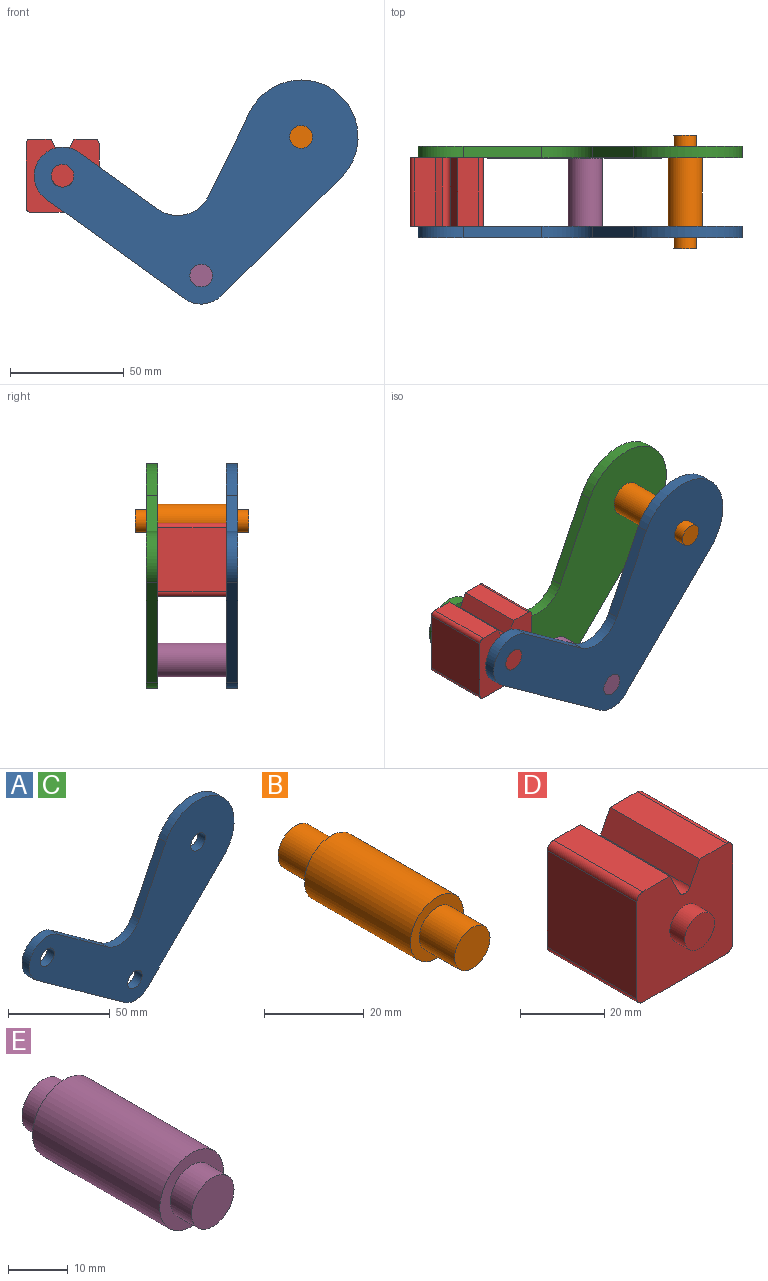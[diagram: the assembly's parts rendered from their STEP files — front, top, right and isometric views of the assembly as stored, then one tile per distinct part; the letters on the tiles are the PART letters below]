
ASSEMBLY  parts=5 mates=2
PART A: 13 faces, bbox 142.2x5x98.4 mm
  f0: plane 52.61x51.97mm, normal (0.7,0,-0.71), area 369.8mm2, adj f1,f9,f11,f12
  f1: cylinder r=25mm len=47.44mm, axis (0,-1,0), area 434.6mm2, adj f0,f2,f11,f12
  f2: plane 37.17x18.26mm, normal (-0.9,0,0.44), area 207.1mm2, adj f1,f3,f11,f12
  f3: cylinder r=15mm len=22.23mm, axis (0,-1,0), area 130.4mm2, adj f2,f4,f11,f12
  f4: plane 34.46x24.81mm, normal (0.58,0,0.81), area 212.3mm2, adj f3,f5,f11,f12
  f5: cylinder r=12.5mm len=22.64mm, axis (0,-1,0), area 196.3mm2, adj f4,f6,f11,f12
  f6: plane 60.86x43.82mm, normal (-0.58,0,-0.81), area 375mm2, adj f5,f9,f11,f12
  f7: cylinder r=5mm len=10mm, axis (0,-1,0), area 157.1mm2, adj f11,f12
  f8: cylinder r=5mm len=10mm, axis (0,-1,0), area 157.1mm2, adj f11,f12
  f9: cylinder r=12.5mm len=16.09mm, axis (0,-1,0), area 87.7mm2, adj f0,f6,f11,f12
  f10: cylinder r=5mm len=10mm, axis (0,-1,0), area 157.1mm2, adj f11,f12
  f11: plane 142.19x98.36mm, normal (0,1,0), area 5739.8mm2, adj f0,f1,f2,f3,f4,f5,f6,f7
  f12: plane 142.19x98.36mm, normal (0,-1,0), area 5739.8mm2, adj f0,f1,f2,f3,f4,f5,f6,f7
PART B: 7 faces, bbox 15x50x15 mm
  f0: cylinder r=7.5mm len=30mm, axis (0,-1,0), area 1413.7mm2, adj f2,f5
  f1: cylinder r=5mm len=10mm, axis (0,1,0), area 314.2mm2, adj f2,f3
  f2: plane 15x15mm, normal (0,-1,0), area 98.2mm2, adj f0,f1
  f3: plane 10x10mm, normal (0,-1,0), area 78.5mm2, adj f1
  f4: cylinder r=5mm len=10mm, axis (0,-1,0), area 314.2mm2, adj f5,f6
  f5: plane 15x15mm, normal (0,1,0), area 98.2mm2, adj f0,f4
  f6: plane 10x10mm, normal (0,1,0), area 78.5mm2, adj f4
PART C: same geometry as A
PART D: 18 faces, bbox 32.1x40x32.1 mm
  f0: plane 30x6.42mm, normal (0.89,0,0.45), area 215.4mm2, adj f4,f6,f10,f13
  f1: plane 30x6.42mm, normal (-0.89,0,0.45), area 215.4mm2, adj f2,f4,f10,f13
  f2: plane 30x9.04mm, normal (0,0,1), area 271.2mm2, adj f1,f4,f10,f14
  f3: plane 30x28.08mm, normal (1,0,0), area 842.3mm2, adj f4,f10,f14,f15
  f4: plane 32.08x32.08mm, normal (0,-1,0), area 900.6mm2, adj f0,f1,f2,f3,f5,f6,f7,f9
  f5: plane 30x28.08mm, normal (0,0,-1), area 842.3mm2, adj f4,f10,f15,f16
  f6: plane 30x9.04mm, normal (0,0,1), area 271.2mm2, adj f0,f4,f10,f17
  f7: plane 30x28.08mm, normal (-1,0,0), area 842.3mm2, adj f4,f10,f16,f17
  f8: plane 10x10mm, normal (0,-1,0), area 78.5mm2, adj f9
  f9: cylinder r=5mm len=10mm, axis (0,1,0), area 157.1mm2, adj f4,f8
  f10: plane 32.08x32.08mm, normal (0,1,0), area 900.6mm2, adj f0,f1,f2,f3,f5,f6,f7,f12
  f11: plane 10x10mm, normal (0,1,0), area 78.5mm2, adj f12
  f12: cylinder r=5mm len=10mm, axis (0,-1,0), area 157.1mm2, adj f10,f11
  f13: cylinder r=2mm len=30mm, axis (0,1,0), area 132.9mm2, adj f0,f1,f4,f10
  f14: cylinder r=2mm len=30mm, axis (0,1,0), area 94.2mm2, adj f2,f3,f4,f10
  f15: cylinder r=2mm len=30mm, axis (0,-1,0), area 94.2mm2, adj f3,f4,f5,f10
  f16: cylinder r=2mm len=30mm, axis (0,1,0), area 94.2mm2, adj f4,f5,f7,f10
  f17: cylinder r=2mm len=30mm, axis (0,-1,0), area 94.2mm2, adj f4,f6,f7,f10
PART E: 7 faces, bbox 15x40x15 mm
  f0: cylinder r=7.5mm len=30mm, axis (0,-1,0), area 1413.7mm2, adj f2,f5
  f1: cylinder r=5mm len=10mm, axis (0,-1,0), area 157.1mm2, adj f2,f3
  f2: plane 15x15mm, normal (0,-1,0), area 98.2mm2, adj f0,f1
  f3: plane 10x10mm, normal (0,-1,0), area 78.5mm2, adj f1
  f4: cylinder r=5mm len=10mm, axis (0,1,0), area 157.1mm2, adj f5,f6
  f5: plane 15x15mm, normal (0,1,0), area 98.2mm2, adj f0,f4
  f6: plane 10x10mm, normal (0,1,0), area 78.5mm2, adj f4
PLACE A t=(0,-20,0)mm
PLACE B t=(0,-20,0)mm fixed
PLACE C t=(0,15,0)mm
PLACE D t=(0,-20,0)mm
PLACE E t=(0,-20,0)mm
MATE revolute D.f9 <-> A.f5  axis (0,1,0) through (-104.69,-17.5,-17.04)mm
MATE fastened C.f7 <-> E.f0  axis (0,-1,0) through (-43.82,20,-60.86)mm
